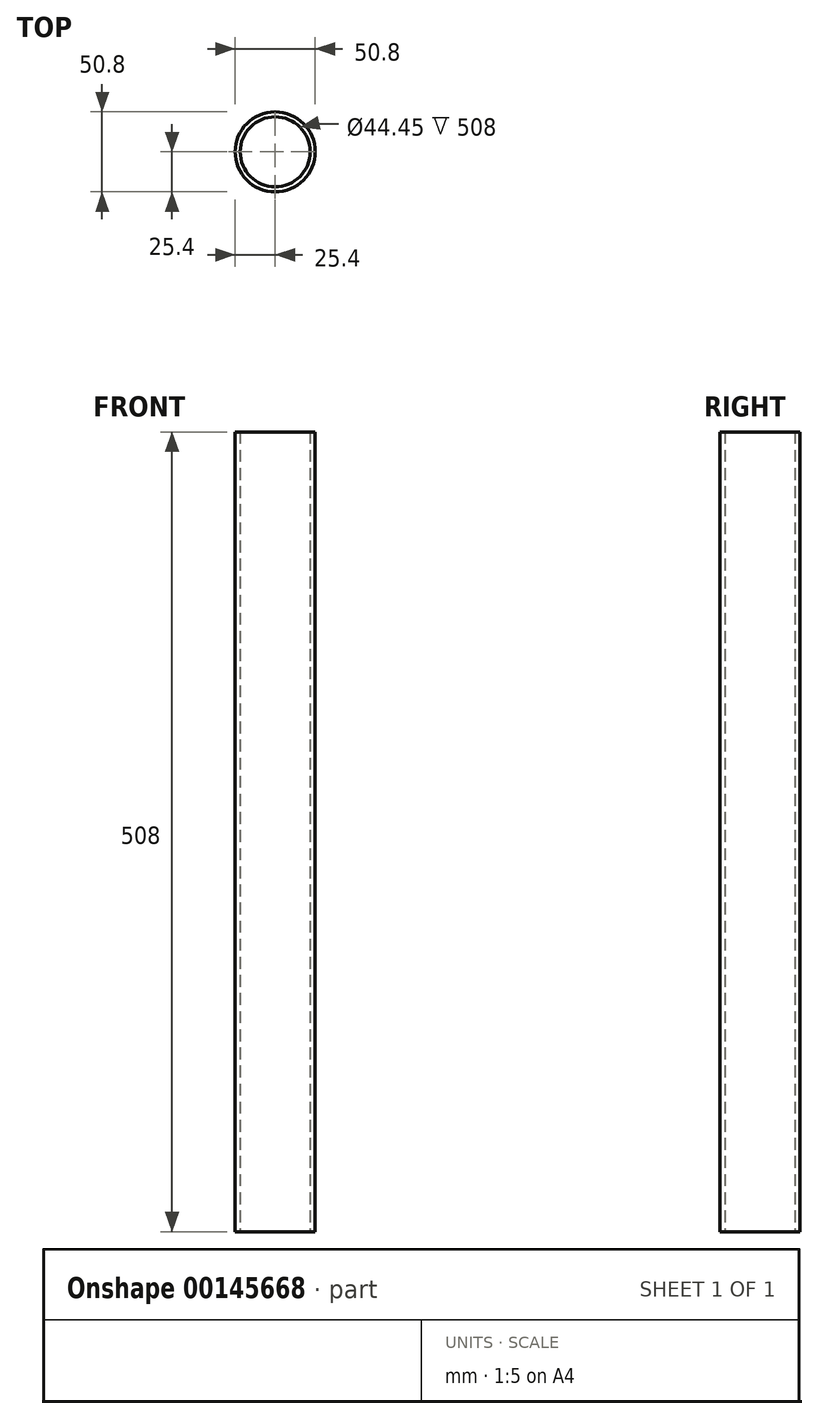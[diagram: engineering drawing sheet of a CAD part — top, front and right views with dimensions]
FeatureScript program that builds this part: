
annotation { "Feature Type Name" : "Feature", "Feature Type Description" : "" }
export const myFeature = defineFeature(function(context is Context, id is Id, definition is map)
    precondition{}
    {
        {
            var Q0;
            Q0=qCreatedBy(makeId("Top.planeOp"),FACE);
            var sketch = newSketch(context, id + "F0", { "sketchPlane" : qUnion([Q0])});
            skCircle(sketch, "E0", {"center": v(0, 0) * mm, "radius": 25.4 * mm});
            skCircle(sketch, "E1", {"center": v(0, 0) * mm, "radius": 22.23 * mm});
            skSolve(sketch);
        }
        {
            var Q0;
            Q0 = qSketchRegion(id + "F0", true);
            extrude(context, id + "F1", {"entities" : qUnion([Q0]), "depth" : 508 * mm});
        }
    });
